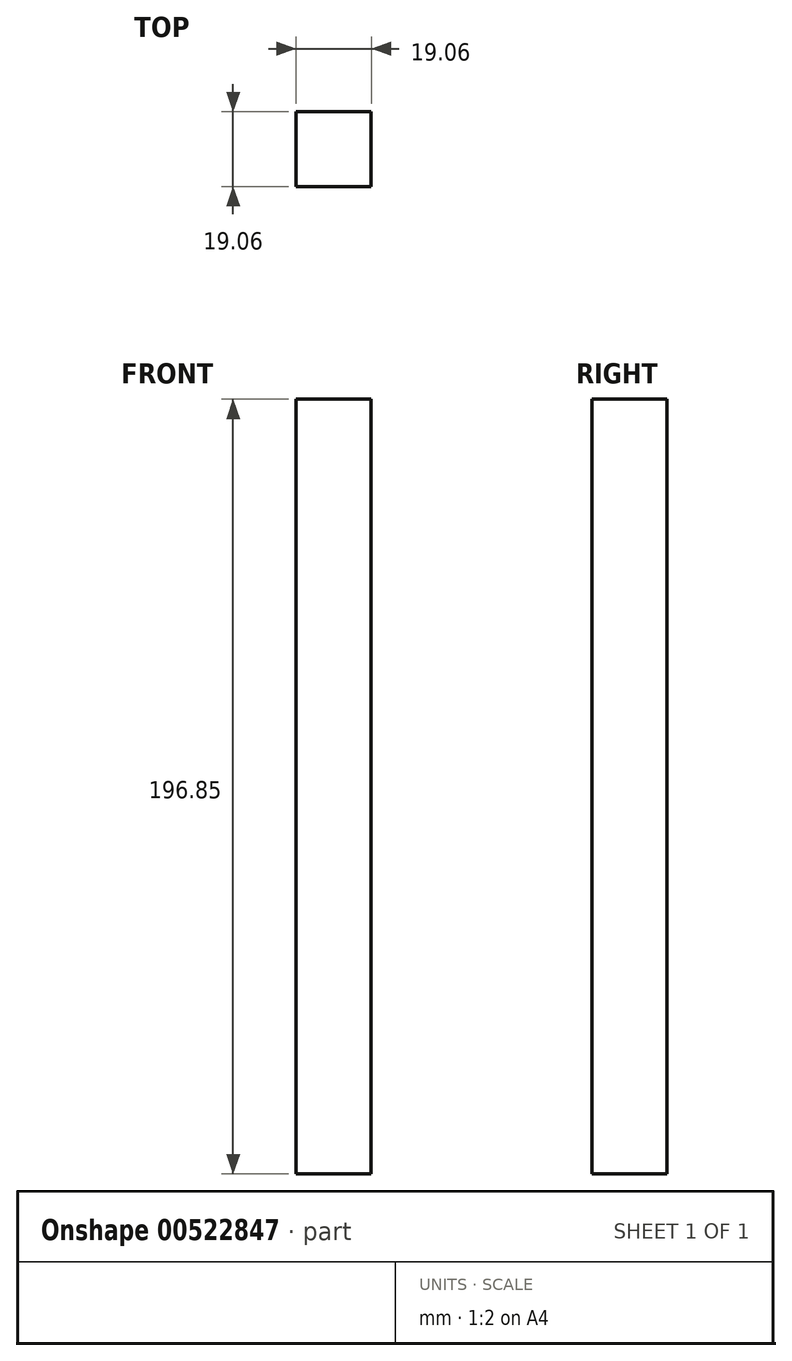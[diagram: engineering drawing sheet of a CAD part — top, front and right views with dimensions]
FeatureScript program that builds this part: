
annotation { "Feature Type Name" : "Feature", "Feature Type Description" : "" }
export const myFeature = defineFeature(function(context is Context, id is Id, definition is map)
    precondition{}
    {
        {
            var Q0;
            Q0=qCreatedBy(makeId("Top.planeOp"),FACE);
            var sketch = newSketch(context, id + "F0", { "sketchPlane" : qUnion([Q0])});
            skLineSegment(sketch, "E0.bottom", {"start": v(-9.52, 9.53) * mm, "end": v(9.53, 9.53) * mm});
            skLineSegment(sketch, "E0.top", {"start": v(-9.53, -9.52) * mm, "end": v(9.53, -9.52) * mm});
            skLineSegment(sketch, "E0.left", {"start": v(-9.53, 9.53) * mm, "end": v(-9.53, -9.52) * mm});
            skLineSegment(sketch, "E0.right", {"start": v(9.53, 9.53) * mm, "end": v(9.53, -9.52) * mm});
            skPoint(sketch, "E0.middle", {"position": v(0, 0) * mm});
            skSolve(sketch);
        }
        {
            var Q0;
            Q0=makeQuery(id+"F0.imprint","IMPRINT",FACE,{"disambiguationData":[TD([[makeQuery(id+"F0.imprint","IMPRINT",EDGE,{"derivedFrom":sQuery(id+"F0.wireOp",EDGE,"E0.bottom")}),-1.0]])]});
            extrude(context, id + "F1", {"entities" : qUnion([Q0]), "depth" : 196.85 * mm, "offsetDistance" : 25.4 * mm});
        }
    });
